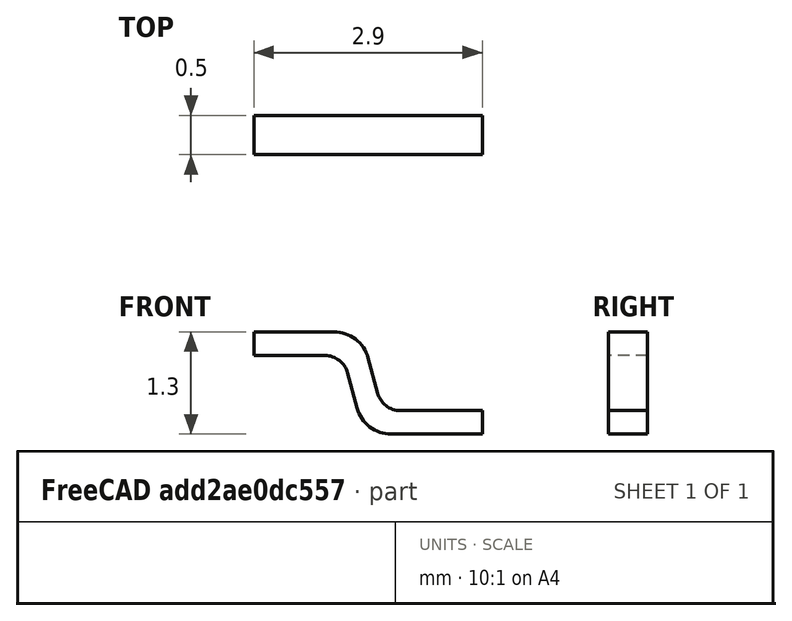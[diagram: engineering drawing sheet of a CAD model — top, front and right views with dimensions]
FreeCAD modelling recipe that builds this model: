
FCSTD DOCUMENT  (FreeCAD 0.18.4R)
Label: Amphenol_C707_10M006_052_2-package_pin
License: All rights reserved
LicenseURL: http://en.wikipedia.org/wiki/All_rights_reserved
objects: Sketcher::SketchObject×1, PartDesign::Pad×1, PartDesign::Body×1
note: 4 computed .brp shape members not serialized (recipe doc carries the construction recipe); baked Part::Feature solids carry a one-line shape summary decoded from their .brp

FEATURE [Sketcher::SketchObject] Sketch
  MapMode = 5
  Placement = pos=(0,0,0) rot=(1,0,0;1.5708rad)
  Support = -> [XZ_Plane]
  sketch-geometry (13):
    g0: LineSegment StartX=0 StartY=1 StartZ=0 EndX=0.9 EndY=1 EndZ=0
    g1: LineSegment StartX=1.18978 StartY=0.777646 StartZ=0 EndX=1.30878 EndY=0.333531 EndZ=0
    g2: LineSegment StartX=1.74344 StartY=0 StartZ=0 EndX=2.9 EndY=0 EndZ=0
    g3: LineSegment StartX=2.9 StartY=0 StartZ=0 EndX=2.9 EndY=0.3 EndZ=0
    g4: LineSegment StartX=2.9 StartY=0.3 StartZ=0 EndX=1.85854 EndY=0.3 EndZ=0
    g5: LineSegment StartX=1.56877 StartY=0.522354 StartZ=0 EndX=1.44977 EndY=0.966469 EndZ=0
    g6: LineSegment StartX=1.0151 StartY=1.3 StartZ=0 EndX=0 EndY=1.3 EndZ=0
    g7: LineSegment StartX=0 StartY=1.3 StartZ=0 EndX=0 EndY=1 EndZ=0
    g8: ArcOfCircle CenterX=1.74344 CenterY=0.45 CenterZ=0 NormalX=0 NormalY=0 NormalZ=1 AngleXU=0 Radius=0.45 StartAngle=3.40339 EndAngle=4.71239
    g9: ArcOfCircle CenterX=0.9 CenterY=0.7 CenterZ=0 NormalX=0 NormalY=0 NormalZ=1 AngleXU=0 Radius=0.3 StartAngle=0.261799 EndAngle=1.5708
    g10: ArcOfCircle CenterX=1.0151 CenterY=0.85 CenterZ=0 NormalX=0 NormalY=0 NormalZ=1 AngleXU=0 Radius=0.45 StartAngle=0.261799 EndAngle=1.5708
    g11: ArcOfCircle CenterX=1.85854 CenterY=0.6 CenterZ=0 NormalX=0 NormalY=0 NormalZ=1 AngleXU=0 Radius=0.3 StartAngle=3.40339 EndAngle=4.71239
    g12: LineSegment [constr] StartX=1.25062 StartY=0.550567 StartZ=0 EndX=1.5404 EndY=0.628213 EndZ=0
  constraints (35):
    c: Horizontal(g0)
    c: PointOnObject(g2,g-1)
    c: Horizontal(g2)
    c: Coincident(g2,g3)
    c: Vertical(g3)
    c: Coincident(g3,g4)
    c: Horizontal(g4)
    c: PointOnObject(g6,g-2)
    c: Horizontal(g6)
    c: Coincident(g6,g7)
    c: Coincident(g0,g7)
    c: Vertical(g7)
    c: Parallel(g1,g5)
    c: Tangent(g1,g8) = -1.5708
    c: Tangent(g2,g8) = -1.5708
    c: Tangent(g0,g9) = 1.5708
    c: Tangent(g1,g9) = 1.5708
    c: Tangent(g5,g10) = -1.5708
    c: Tangent(g6,g10) = -1.5708
    c: Tangent(g4,g11) = 1.5708
    c: Tangent(g5,g11) = 1.5708
    c: DistanceY(g3,g3) = 0.3
    c: DistanceY(g7,g7) = 0.3
    c: DistanceX(g0,g0) = 0.9
    c: DistanceY(g-1,g0) = 1
    c: DistanceX(g-1,g2) = 2.9
    c: Equal(g9,g11)
    c: Equal(g10,g8)
    c: PointOnObject(g12,g5)
    c: Perpendicular(g12,g1)
    c: Distance(g12) = 0.3
    c: Angle(g1,g-1) = 1.309
    c: Radius(g8) = 0.45
    c: Radius(g9) = 0.3
    c: PointOnObject(g12,g1)
FEATURE [PartDesign::Pad] Pad  label="Pin_Pad"
  Length = 0.5
  Length2 = 100
  Midplane = true
  Placement = pos=(0,0,0) rot=(1,0,0;1.5708rad)
  Profile = -> Sketch
  Type = 0
FEATURE [PartDesign::Body] Body  label="Package_pin"
  Group = -> [Sketch,Pad]
  Origin = -> Origin
  Tip = -> Pad
